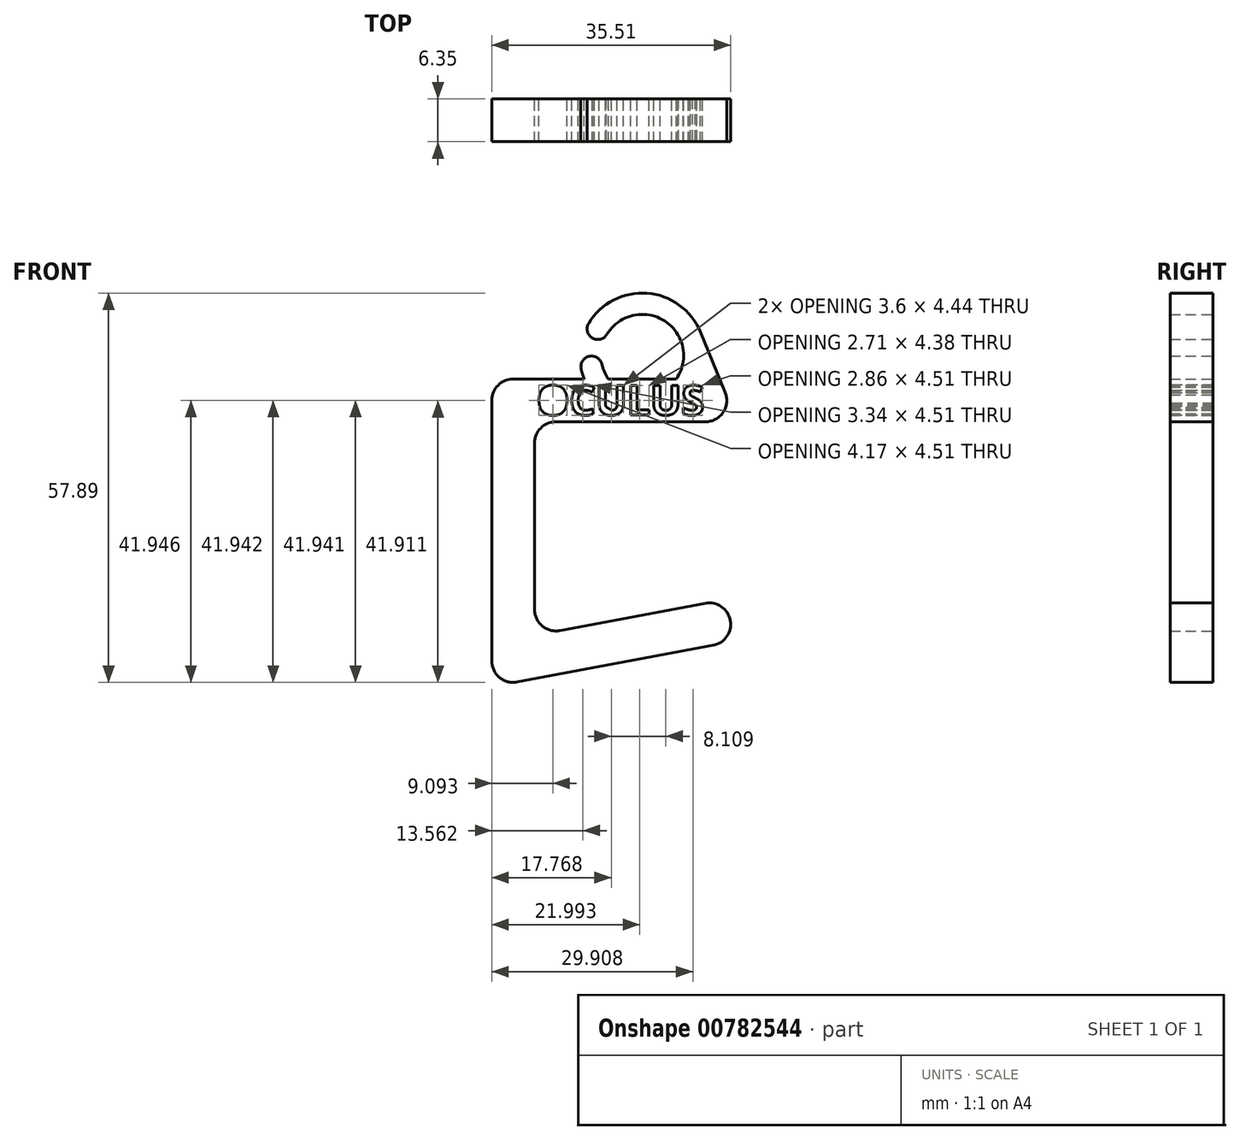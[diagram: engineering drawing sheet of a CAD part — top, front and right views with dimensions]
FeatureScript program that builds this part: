
annotation { "Feature Type Name" : "Feature", "Feature Type Description" : "" }
export const myFeature = defineFeature(function(context is Context, id is Id, definition is map)
    precondition{}
    {
        {
            var Q0;
            Q0=qCreatedBy(makeId("Front.planeOp"),FACE);
            var sketch = newSketch(context, id + "F0", { "sketchPlane" : qUnion([Q0])});
            skLineSegment(sketch, "E0", {"start": v(0, -3.18) * mm, "end": v(0, -27.92) * mm});
            skLineSegment(sketch, "E1", {"start": v(3.76, -31.04) * mm, "end": v(25.4, -26.99) * mm});
            skLineSegment(sketch, "E2", {"start": v(3.18, 0) * mm, "end": v(25.4, 0) * mm});
            skLineSegment(sketch, "E3.0", {"start": v(-2.59, -38.7) * mm, "end": v(26.57, -33.23) * mm});
            skLineSegment(sketch, "E3.1", {"start": v(-6.35, 3.17) * mm, "end": v(-6.35, -35.58) * mm});
            skLineSegment(sketch, "E3.2", {"start": v(-3.17, 6.35) * mm, "end": v(25.4, 6.35) * mm});
            skArc(sketch, "E4", {"start": v(25.4, 6.35) * mm, "mid": v(28.57, 3.17) * mm, "end": v(25.4, 0) * mm});
            skArc(sketch, "E5", {"start": v(25.4, -26.99) * mm, "mid": v(29.1, -29.52) * mm, "end": v(26.57, -33.23) * mm});
            skPoint(sketch, "E6.visualSharp", {"position": v(0, -31.75) * mm});
            skArc(sketch, "E6.filletArc", {"start": v(0, -27.92) * mm, "mid": v(1.15, -30.37) * mm, "end": v(3.76, -31.04) * mm});
            skPoint(sketch, "E7.visualSharp", {"position": v(0, 0) * mm});
            skArc(sketch, "E7.filletArc", {"start": v(3.18, 0) * mm, "mid": v(0.93, -0.93) * mm, "end": v(0, -3.18) * mm});
            skPoint(sketch, "E8.visualSharp", {"position": v(-6.35, -39.4) * mm});
            skArc(sketch, "E8.filletArc", {"start": v(-6.35, -35.58) * mm, "mid": v(-5.2, -38.02) * mm, "end": v(-2.59, -38.7) * mm});
            skPoint(sketch, "E9.visualSharp", {"position": v(-6.35, 6.35) * mm});
            skArc(sketch, "E9.filletArc", {"start": v(-3.17, 6.35) * mm, "mid": v(-5.42, 5.42) * mm, "end": v(-6.35, 3.17) * mm});
            skArc(sketch, "E10", {"start": v(10.03, 8.52) * mm, "mid": v(22.08, 8.83) * mm, "end": v(10.77, 13) * mm});
            skArc(sketch, "E11.0", {"start": v(6.93, 7.84) * mm, "mid": v(25.2, 8.31) * mm, "end": v(8.05, 14.63) * mm});
            skLineSegment(sketch, "E12", {"start": v(10.03, 8.52) * mm, "end": v(6.93, 7.84) * mm});
            skLineSegment(sketch, "E13", {"start": v(10.77, 13) * mm, "end": v(8.05, 14.63) * mm});
            skArc(sketch, "E14", {"start": v(10.03, 8.52) * mm, "mid": v(8.14, 9.73) * mm, "end": v(6.93, 7.84) * mm});
            skArc(sketch, "E15", {"start": v(8.05, 14.63) * mm, "mid": v(8.59, 12.45) * mm, "end": v(10.77, 13) * mm});
            skLineSegment(sketch, "E16", {"start": v(24.63, 13.37) * mm, "end": v(28.57, 3.8) * mm});
            skPoint(sketch, "E16.endSnap0", {"position": v(28.57, 3.17) * mm});
            skText(sketch, "E17", { "text": "OCULUS", "fontName": "OpenSans-Bold.ttf"});
            skPoint(sketch, "E17.firstSnap0", {"position": v(-5.42, 5.42) * mm});
            const initialGuessF0  = {"E17": [0.0003, 0.001, 1, 0, 0.00442]};
            skSetInitialGuess(sketch, initialGuessF0);
            skSolve(sketch);
        }
        {
            var Q0;
            Q0 = qSketchRegion(id + "F0", true);
            extrude(context, id + "F1", {"entities" : qUnion([Q0]), "depth" : 6.35 * mm, "offsetDistance" : 25.4 * mm});
        }
        {
            var Q0;
            {var subQ2=sQuery(id+"F0.wireOp",EDGE,"E17.sketch_text.stroke-30");Q0=makeQuery(id+"F0.imprint","IMPRINT",FACE,{"disambiguationData":[TD([[makeQuery(id+"F0.imprint","IMPRINT",EDGE,{"derivedFrom":subQ2}),1.0]])]});}
            extrude(context, id + "F2", {"entities" : qUnion([Q0]), "operationType" : NewBodyOperationType.ADD, "depth" : 6.35 * mm, "offsetDistance" : 25.4 * mm});
        }
        {
            var Q0;
            {var subQ0=sQuery(id+"F0.wireOp",EDGE,"E17.sketch_text.stroke-86");Q0=makeQuery(id+"F0.imprint","IMPRINT",FACE,{"disambiguationData":[TD([[makeQuery(id+"F0.imprint","IMPRINT",EDGE,{"derivedFrom":subQ0}),1.0]])]});}
            extrude(context, id + "F3", {"entities" : qUnion([Q0]), "operationType" : NewBodyOperationType.ADD, "depth" : 6.35 * mm, "offsetDistance" : 25.4 * mm});
        }
    });
